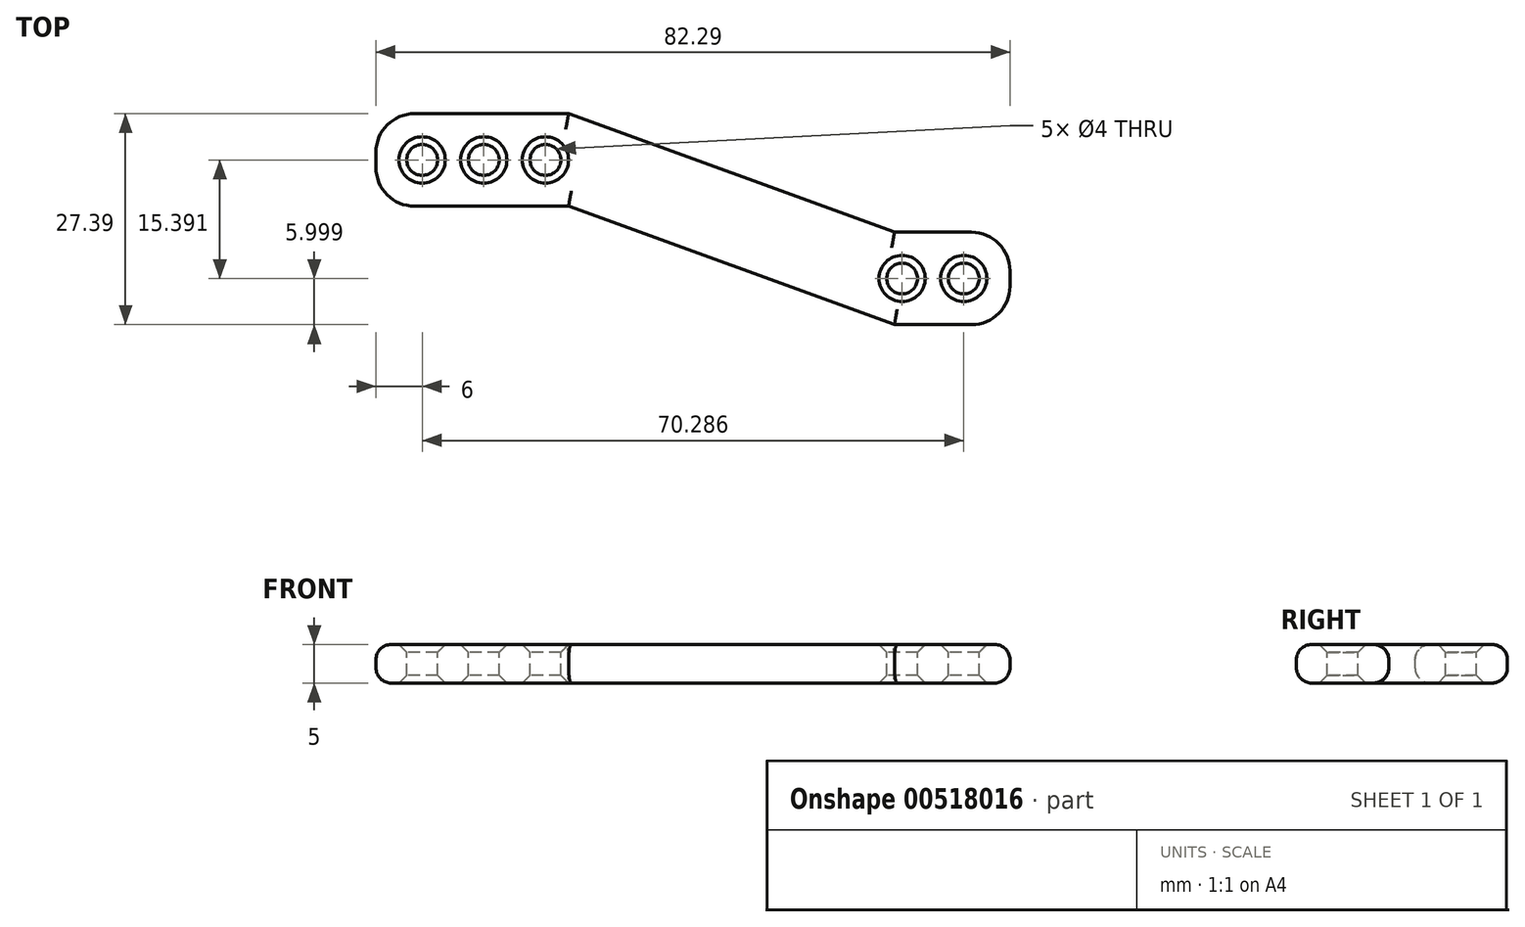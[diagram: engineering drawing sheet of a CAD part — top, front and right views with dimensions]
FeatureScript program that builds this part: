
annotation { "Feature Type Name" : "Feature", "Feature Type Description" : "" }
export const myFeature = defineFeature(function(context is Context, id is Id, definition is map)
    precondition{}
    {
        {
            var Q0;
            Q0=qCreatedBy(makeId("Top.planeOp"),FACE);
            var sketch = newSketch(context, id + "F0", { "sketchPlane" : qUnion([Q0])});
            skLineSegment(sketch, "E0.bottom", {"start": v(0, 0) * mm, "end": v(25, 0) * mm});
            skLineSegment(sketch, "E0.top", {"start": v(0, -12) * mm, "end": v(25, -12) * mm});
            skLineSegment(sketch, "E0.left", {"start": v(0, 0) * mm, "end": v(0, -12) * mm});
            skLineSegment(sketch, "E0.right", {"start": v(25, 0) * mm, "end": v(25, -12) * mm});
            skLineSegment(sketch, "E1", {"start": v(25, -12) * mm, "end": v(67.29, -27.4) * mm});
            skLineSegment(sketch, "E2", {"start": v(25, 0) * mm, "end": v(67.29, -15.4) * mm});
            skLineSegment(sketch, "E3", {"start": v(67.29, -15.4) * mm, "end": v(67.29, -27.4) * mm});
            skLineSegment(sketch, "E4.bottom", {"start": v(67.29, -15.4) * mm, "end": v(67.29, -15.4) * mm});
            skLineSegment(sketch, "E4.top", {"start": v(67.29, -27.4) * mm, "end": v(67.29, -27.4) * mm});
            skLineSegment(sketch, "E5.bottom", {"start": v(67.29, -15.4) * mm, "end": v(82.29, -15.4) * mm});
            skLineSegment(sketch, "E5.top", {"start": v(67.29, -27.4) * mm, "end": v(82.29, -27.4) * mm});
            skLineSegment(sketch, "E5.right", {"start": v(82.29, -15.4) * mm, "end": v(82.29, -27.4) * mm});
            skSolve(sketch);
        }
        {
            var Q0;
            Q0 = qSketchRegion(id + "F0", true);
            extrude(context, id + "F1", {"entities" : qUnion([Q0]), "depth" : 5 * mm, "offsetDistance" : 25 * mm});
        }
        {
            var Q0;
            Q0=makeQuery(id+"F1.opExtrude","CAP_FACE",FACE,{"disambiguationData":[OSD([sQuery(id+"F0.wireOp",EDGE,"E0.bottom"),sQuery(id+"F0.wireOp",EDGE,"E0.top"),sQuery(id+"F0.wireOp",EDGE,"E0.left"),sQuery(id+"F0.wireOp",EDGE,"E1"),sQuery(id+"F0.wireOp",EDGE,"E2"),sQuery(id+"F0.wireOp",EDGE,"E5.bottom"),sQuery(id+"F0.wireOp",EDGE,"E5.top"),sQuery(id+"F0.wireOp",EDGE,"E5.right")])],"isStart":false});
            var sketch = newSketch(context, id + "F2", { "sketchPlane" : qUnion([Q0])});
            skCircle(sketch, "E6", {"center": v(6, -6) * mm, "radius": 2 * mm});
            skPoint(sketch, "E6.centerSnap0", {"position": v(12.5, 0) * mm});
            skCircle(sketch, "E7", {"center": v(76.29, -21.4) * mm, "radius": 2 * mm});
            skCircle(sketch, "E8.1.0.0", {"center": v(14, -6) * mm, "radius": 2 * mm});
            skCircle(sketch, "E8.2.0.0", {"center": v(22, -6) * mm, "radius": 2 * mm});
            skLineSegment(sketch, "E8.direction1", {"start": v(6, -6) * mm, "end": v(14, -6) * mm, "construction": true});
            skCircle(sketch, "E9.1.0.0", {"center": v(68.29, -21.4) * mm, "radius": 2 * mm});
            skLineSegment(sketch, "E9.direction1", {"start": v(76.29, -21.4) * mm, "end": v(68.29, -21.4) * mm, "construction": true});
            skSolve(sketch);
        }
        {
            var Q0;
            Q0 = qSketchRegion(id + "F2", true);
            extrude(context, id + "F3", {"entities" : qUnion([Q0]), "operationType" : NewBodyOperationType.REMOVE, "endBound" : BoundingType.THROUGH_ALL, "oppositeDirection" : true, "depth" : 25 * mm, "offsetDistance" : 25 * mm});
        }
        {
            var Q0;
            Q0=makeQuery(id+"F1.opExtrude","CAP_EDGE",EDGE,{"disambiguationData":[OSD([sQuery(id+"F0.wireOp",EDGE,"E2")])],"isStart":false});
            var Q1;
            Q1=makeQuery(id+"F1.opExtrude","CAP_EDGE",EDGE,{"disambiguationData":[OSD([sQuery(id+"F0.wireOp",EDGE,"E5.bottom")])],"isStart":false});
            var Q2;
            Q2=makeQuery(id+"F1.opExtrude","CAP_EDGE",EDGE,{"disambiguationData":[OSD([sQuery(id+"F0.wireOp",EDGE,"E5.right")])],"isStart":false});
            var Q3;
            Q3=makeQuery(id+"F1.opExtrude","CAP_EDGE",EDGE,{"disambiguationData":[OSD([sQuery(id+"F0.wireOp",EDGE,"E5.top")])],"isStart":false});
            var Q4;
            Q4=makeQuery(id+"F1.opExtrude","CAP_EDGE",EDGE,{"disambiguationData":[OSD([sQuery(id+"F0.wireOp",EDGE,"E1")])],"isStart":false});
            var Q5;
            Q5=makeQuery(id+"F1.opExtrude","CAP_EDGE",EDGE,{"disambiguationData":[OSD([sQuery(id+"F0.wireOp",EDGE,"E0.top")])],"isStart":false});
            var Q6;
            Q6=makeQuery(id+"F1.opExtrude","CAP_EDGE",EDGE,{"disambiguationData":[OSD([sQuery(id+"F0.wireOp",EDGE,"E0.left")])],"isStart":false});
            var Q7;
            Q7=makeQuery(id+"F1.opExtrude","CAP_EDGE",EDGE,{"disambiguationData":[OSD([sQuery(id+"F0.wireOp",EDGE,"E0.bottom")])],"isStart":false});
            var Q8;
            Q8=makeQuery(id+"F1.opExtrude","CAP_EDGE",EDGE,{"disambiguationData":[OSD([sQuery(id+"F0.wireOp",EDGE,"E0.top")])],"isStart":true});
            var Q9;
            Q9=makeQuery(id+"F1.opExtrude","CAP_EDGE",EDGE,{"disambiguationData":[OSD([sQuery(id+"F0.wireOp",EDGE,"E0.left")])],"isStart":true});
            var Q10;
            Q10=makeQuery(id+"F1.opExtrude","CAP_EDGE",EDGE,{"disambiguationData":[OSD([sQuery(id+"F0.wireOp",EDGE,"E0.bottom")])],"isStart":true});
            var Q11;
            Q11=makeQuery(id+"F1.opExtrude","CAP_EDGE",EDGE,{"disambiguationData":[OSD([sQuery(id+"F0.wireOp",EDGE,"E2")])],"isStart":true});
            var Q12;
            Q12=makeQuery(id+"F1.opExtrude","CAP_EDGE",EDGE,{"disambiguationData":[OSD([sQuery(id+"F0.wireOp",EDGE,"E1")])],"isStart":true});
            var Q13;
            Q13=makeQuery(id+"F1.opExtrude","CAP_EDGE",EDGE,{"disambiguationData":[OSD([sQuery(id+"F0.wireOp",EDGE,"E5.top")])],"isStart":true});
            var Q14;
            Q14=makeQuery(id+"F1.opExtrude","CAP_EDGE",EDGE,{"disambiguationData":[OSD([sQuery(id+"F0.wireOp",EDGE,"E5.bottom")])],"isStart":true});
            var Q15;
            Q15=makeQuery(id+"F1.opExtrude","CAP_EDGE",EDGE,{"disambiguationData":[OSD([sQuery(id+"F0.wireOp",EDGE,"E5.right")])],"isStart":true});
            fillet(context, id + "F4", {"entities" : qUnion([Q0, Q1, Q2, Q3, Q4, Q5, Q6, Q7, Q8, Q9, Q10, Q11, Q12, Q13, Q14, Q15]), "radius" : 2 * mm, "tangentPropagation" : true, "allowEdgeOverflow" : false});
        }
        {
            var Q0;
            Q0=makeQuery(id+"F4.opFillet","BLEND_EDGE",EDGE,{"blendedFrom":[makeQuery(id+"F1.opExtrude","CAP_EDGE",EDGE,{"disambiguationData":[OSD([sQuery(id+"F0.wireOp",EDGE,"E0.bottom")])],"isStart":true}),makeQuery(id+"F1.opExtrude","CAP_EDGE",EDGE,{"disambiguationData":[OSD([sQuery(id+"F0.wireOp",EDGE,"E0.left")])],"isStart":true})],"blendedInto":[]});
            var Q1;
            Q1=makeQuery(id+"F4.opFillet","BLEND_EDGE",EDGE,{"blendedFrom":[makeQuery(id+"F1.opExtrude","CAP_EDGE",EDGE,{"disambiguationData":[OSD([sQuery(id+"F0.wireOp",EDGE,"E0.top")])],"isStart":true}),makeQuery(id+"F1.opExtrude","CAP_EDGE",EDGE,{"disambiguationData":[OSD([sQuery(id+"F0.wireOp",EDGE,"E0.left")])],"isStart":true})],"blendedInto":[]});
            var Q2;
            Q2=makeQuery(id+"F4.opFillet","BLEND_EDGE",EDGE,{"blendedFrom":[makeQuery(id+"F1.opExtrude","CAP_EDGE",EDGE,{"disambiguationData":[OSD([sQuery(id+"F0.wireOp",EDGE,"E5.top")])],"isStart":true}),makeQuery(id+"F1.opExtrude","CAP_EDGE",EDGE,{"disambiguationData":[OSD([sQuery(id+"F0.wireOp",EDGE,"E5.right")])],"isStart":true})],"blendedInto":[]});
            var Q3;
            Q3=makeQuery(id+"F4.opFillet","BLEND_EDGE",EDGE,{"blendedFrom":[makeQuery(id+"F1.opExtrude","CAP_EDGE",EDGE,{"disambiguationData":[OSD([sQuery(id+"F0.wireOp",EDGE,"E5.bottom")])],"isStart":true}),makeQuery(id+"F1.opExtrude","CAP_EDGE",EDGE,{"disambiguationData":[OSD([sQuery(id+"F0.wireOp",EDGE,"E5.right")])],"isStart":true})],"blendedInto":[]});
            fillet(context, id + "F5", {"entities" : qUnion([Q0, Q1, Q2, Q3]), "radius" : 5 * mm, "tangentPropagation" : true, "allowEdgeOverflow" : false});
        }
        {
            var Q0;
            Q0=makeQuery(id+"F3.boolean.opBoolean","COPY",FACE,{"derivedFrom":makeQuery(id+"F3.opExtrude","SWEPT_FACE",FACE,{"disambiguationData":[OSD([sQuery(id+"F2.wireOp",EDGE,"E8.2.0.0")])]})});
            var Q1;
            Q1=makeQuery(id+"F3.boolean.opBoolean","COPY",FACE,{"derivedFrom":makeQuery(id+"F3.opExtrude","SWEPT_FACE",FACE,{"disambiguationData":[OSD([sQuery(id+"F2.wireOp",EDGE,"E8.1.0.0")])]})});
            var Q2;
            Q2=makeQuery(id+"F3.boolean.opBoolean","COPY",FACE,{"derivedFrom":makeQuery(id+"F3.opExtrude","SWEPT_FACE",FACE,{"disambiguationData":[OSD([sQuery(id+"F2.wireOp",EDGE,"E6")])]})});
            var Q3;
            Q3=makeQuery(id+"F3.boolean.opBoolean","COPY",FACE,{"derivedFrom":makeQuery(id+"F3.opExtrude","SWEPT_FACE",FACE,{"disambiguationData":[OSD([sQuery(id+"F2.wireOp",EDGE,"E9.1.0.0")])]})});
            var Q4;
            Q4=makeQuery(id+"F3.boolean.opBoolean","COPY",FACE,{"derivedFrom":makeQuery(id+"F3.opExtrude","SWEPT_FACE",FACE,{"disambiguationData":[OSD([sQuery(id+"F2.wireOp",EDGE,"E7")])]})});
            chamfer(context, id + "F6", {"entities" : qUnion([Q0, Q1, Q2, Q3, Q4]), "width" : 1 * mm, "tangentPropagation" : true});
        }
    });
